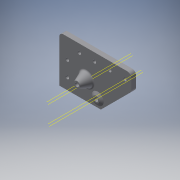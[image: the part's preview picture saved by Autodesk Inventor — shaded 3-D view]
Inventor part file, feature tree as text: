
AUTODESK INVENTOR PART (.ipt)
format: ipt  version: 2018 (Build 220112000, 112)  size: 218,624 bytes
history: native  units: in
note: dims shown in document units (in); Inventor stores cm internally (conversion verified against a paired STEP export)
features: sketch x8, extrude x6, plane x4, revolve x2, fillet x2, projected_geometry x2
ambient origin geometry x8: Origin, YZ Plane, XZ Plane, XY Plane, X Axis, Y Axis, Z Axis, Center Point
bodies: Solid1 (feature_tree)
feature tree (24):
  extrude  "Extrusion1"  Depth=0.7874in
  extrude  "Extrusion2"  Depth=3.5433in
  plane  "Work Plane2"
  revolve  "Revolution1"  [1 undecoded]
  extrude  "Extrusion3"  Depth=0.5512in
  extrude  "Extrusion4"  [1 undecoded]
  fillet  "Fillet1"  Radius=0.3543in
  extrude  "Extrusion5"  TaperAngle=90.0deg  [1 undecoded]
  plane  "Work Plane4"
  revolve  "Revolution2"  [1 undecoded]
  fillet  "Fillet2"  Radius=0.1654in
  extrude  "Extrusion6"  Depth=0.3937in
  sketch  "Sketch1"  dims[d0=0.7874in d1=0.7874in]
  sketch  "Sketch2"  dims[d2=3.5433in d3=3.5433in]
  plane  "Work Plane1"
  sketch  "Sketch3"  dims[d4=0.2362in d5=0.0in d6=0.1969in]
  sketch  "Sketch4"  dims[d7=1.3386in d8=0.5512in]
  projected_geometry  "Projected Loop1"
  sketch  "Sketch5"  dims[d9=0.2362in d10=0.0in d11=-0.0984in d12=0.3543in]
  sketch  "Sketch7"  dims[d13=0.4724in d14=90.0deg]
  plane  "Work Plane3"
  sketch  "Sketch8"  dims[d15=0.2362in d16=0.0in d17=0.1575in d18=0.1654in]
  projected_geometry  "Projected Loop2"
  sketch  "Sketch9"  dims[d19=0.315in d20=0.748in d21=0.748in d22=0.748in d23=0.315in d24=0.748in d25=0.748in d26=0.748in d27=0.2362in d28=0.0in d29=0.0787in d30=0.3543in d32=0.3543in d33=0.1969in d34=0.0in d35=0.0984in d36=0.1969in d37=0.0591in d38=0.0787in d39=90.0deg d40=0.1969in d42=0.3937in d43=0.0in d44=1.2598in]
note: 4 required parameter values undecoded (feature->parameter linkage not recoverable at this tier; creation-order binding heuristic only, values carry confidence <= 0.55)